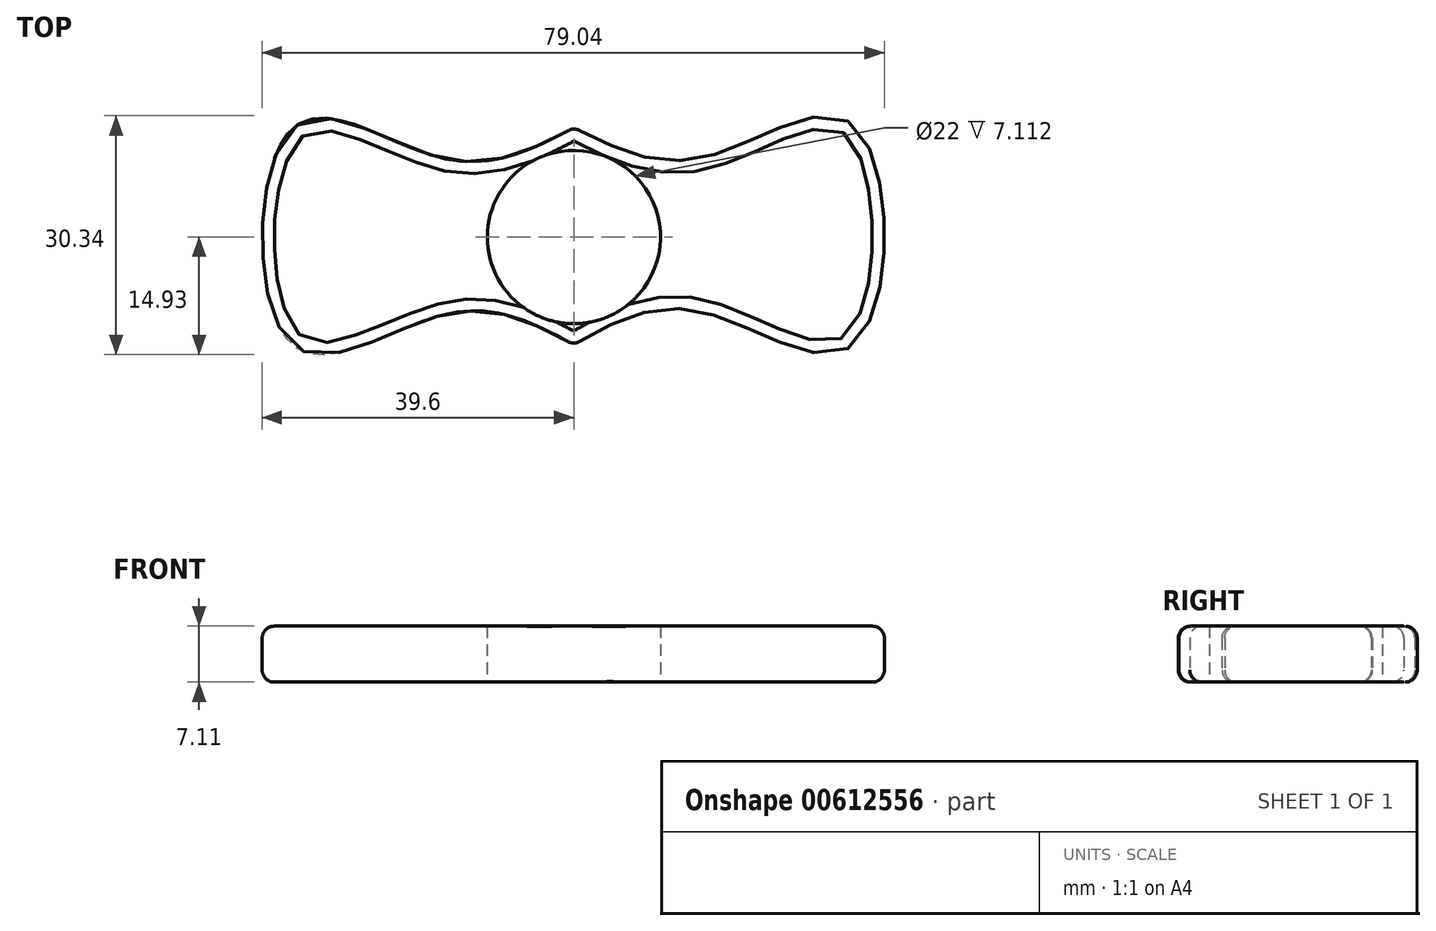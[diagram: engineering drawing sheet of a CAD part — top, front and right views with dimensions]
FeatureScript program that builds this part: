
annotation { "Feature Type Name" : "Feature", "Feature Type Description" : "" }
export const myFeature = defineFeature(function(context is Context, id is Id, definition is map)
    precondition{}
    {
        {
            var Q0;
            Q0=qCreatedBy(makeId("Top.planeOp"),FACE);
            var sketch = newSketch(context, id + "F0", { "sketchPlane" : qUnion([Q0])});
            skCircle(sketch, "E0", {"center": v(0, 0) * mm, "radius": 11 * mm});
            skLineSegment(sketch, "E1.bottom", {"start": v(35.56, -13.71) * mm, "end": v(-35.56, -13.71) * mm});
            skLineSegment(sketch, "E1.top", {"start": v(35.56, 13.71) * mm, "end": v(-35.56, 13.71) * mm});
            skLineSegment(sketch, "E1.left", {"start": v(35.56, -13.71) * mm, "end": v(35.56, 13.71) * mm});
            skLineSegment(sketch, "E1.right", {"start": v(-35.56, -13.71) * mm, "end": v(-35.56, 13.71) * mm});
            skLineSegment(sketch, "E2", {"start": v(0, 0) * mm, "end": v(16.2, 0) * mm});
            skLineSegment(sketch, "E3", {"start": v(16.2, 0) * mm, "end": v(0, 0) * mm});
            skLineSegment(sketch, "E4", {"start": v(0.36, 0.18) * mm, "end": v(-15.85, 0) * mm});
            skLineSegment(sketch, "E5", {"start": v(0.36, 0.18) * mm, "end": v(29.03, 0) * mm});
            skPoint(sketch, "E5.endSnap0", {"position": v(8.1, 0) * mm});
            skLineSegment(sketch, "E6", {"start": v(29.03, 0) * mm, "end": v(0.36, 0.18) * mm});
            skLineSegment(sketch, "E7", {"start": v(0.36, 0.18) * mm, "end": v(-28.31, 0.18) * mm});
            skLineSegment(sketch, "E8", {"start": v(16.2, 0) * mm, "end": v(16.2, -13.71) * mm});
            skLineSegment(sketch, "E9", {"start": v(16.2, -13.71) * mm, "end": v(16.37, 13.71) * mm});
            skLineSegment(sketch, "E10", {"start": v(-15.85, 0) * mm, "end": v(-16, 13.71) * mm});
            skSolve(sketch);
        }
        {
            var Q0;
            Q0=qCreatedBy(makeId("Top.planeOp"),FACE);
            var sketch = newSketch(context, id + "F1", { "sketchPlane" : qUnion([Q0])});
            skFitSpline(sketch, "E11", {"points": [v(0, -13.69) * mm, v(15.99, -9.4) * mm, v(35.5, -13.69) * mm, v(35.5, 14.23) * mm, v(16.46, 10.1) * mm, v(0, 13.92) * mm], "startDerivative": vector(80.95, 46.56) * mm, "endDerivative": vector(-83.43, 43.02) * mm});
            skFitSpline(sketch, "E12", {"points": [v(0, 13.92) * mm, v(-16.38, 9.95) * mm, v(-35.57, 13.92) * mm, v(-35.73, -13.69) * mm, v(-15.9, -9.72) * mm, v(0, -13.69) * mm], "startDerivative": vector(-82.84, -43.73) * mm, "endDerivative": vector(80.5, -43.81) * mm});
            skSolve(sketch);
        }
        {
            var Q0;
            Q0 = qSketchRegion(id + "F1", true);
            extrude(context, id + "F2", {"entities" : qUnion([Q0]), "depth" : 7.11 * mm, "offsetDistance" : 25.4 * mm});
        }
        {
            var Q0;
            Q0=sQuery(id+"F0.wireOp",VERTEX,"E0.center");
            var Q1;
            Q1=makeQuery(id+"F2.opExtrude","SWEPT_BODY",BODY,{"disambiguationData":[OSD([sQuery(id+"F1.wireOp",EDGE,"E11"),sQuery(id+"F1.wireOp",EDGE,"E12")])]});
            hole(context, id + "F3", {"style" : HoleStyle.SIMPLE, "endStyle" : HoleEndStyle.THROUGH, "oppositeDirection" : true, "holeDiameter" : 22 * mm, "majorDiameter" : 6.35 * mm, "isTappedThrough" : true, "tappedDepth" : 12.7 * mm, "tapClearance" : 3, "startFromSketch" : true, "locations" : qUnion([Q0]), "scope" : qUnion([Q1])});
        }
        {
            var Q0;
            Q0=makeQuery(id+"F2.opExtrude","CAP_EDGE",EDGE,{"disambiguationData":[OSD([sQuery(id+"F1.wireOp",EDGE,"E11")])],"isStart":false});
            var Q1;
            Q1=makeQuery(id+"F2.opExtrude","CAP_EDGE",EDGE,{"disambiguationData":[OSD([sQuery(id+"F1.wireOp",EDGE,"E12")])],"isStart":false});
            var Q2;
            Q2=makeQuery(id+"F2.opExtrude","CAP_EDGE",EDGE,{"disambiguationData":[OSD([sQuery(id+"F1.wireOp",EDGE,"E11")])],"isStart":true});
            var Q3;
            Q3=makeQuery(id+"F2.opExtrude","CAP_EDGE",EDGE,{"disambiguationData":[OSD([sQuery(id+"F1.wireOp",EDGE,"E12")])],"isStart":true});
            var Q4;
            {var subQ0=sQuery(id+"F1.wireOp",EDGE,"E12");var subQ1=sQuery(id+"F1.wireOp",EDGE,"E11");Q4=makeQuery(id+"F2.opExtrude","SWEPT_EDGE",EDGE,{"disambiguationData":[OSD([subQ1,subQ0]),TDD([makeQuery(id+"F1.imprint","INTERSECT",VERTEX,{"disambiguationData":[OD(0.0)],"derivedFrom":[subQ1,subQ0]})])]});}
            var Q5;
            {var subQ0=sQuery(id+"F1.wireOp",EDGE,"E12");var subQ1=sQuery(id+"F1.wireOp",EDGE,"E11");Q5=makeQuery(id+"F2.opExtrude","SWEPT_EDGE",EDGE,{"disambiguationData":[OSD([subQ1,subQ0]),TDD([makeQuery(id+"F1.imprint","INTERSECT",VERTEX,{"disambiguationData":[OD(1.0)],"derivedFrom":[subQ1,subQ0]})])]});}
            fillet(context, id + "F4", {"entities" : qUnion([Q0, Q1, Q2, Q3, Q4, Q5]), "radius" : 1.52 * mm, "tangentPropagation" : true, "allowEdgeOverflow" : false});
        }
    });
